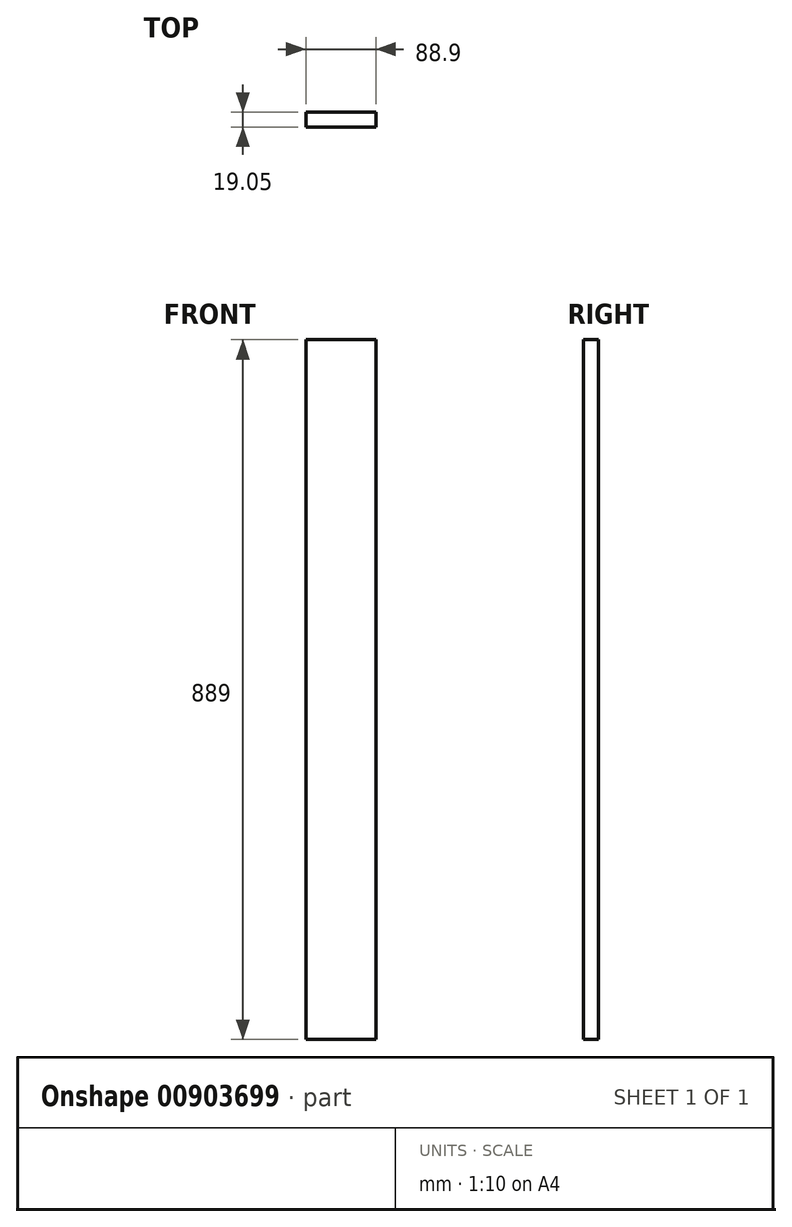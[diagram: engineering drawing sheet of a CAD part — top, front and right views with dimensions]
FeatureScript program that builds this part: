
annotation { "Feature Type Name" : "Feature", "Feature Type Description" : "" }
export const myFeature = defineFeature(function(context is Context, id is Id, definition is map)
    precondition{}
    {
        {
            var Q0;
            Q0=qCreatedBy(makeId("Front.planeOp"),FACE);
            var sketch = newSketch(context, id + "F0", { "sketchPlane" : qUnion([Q0])});
            skLineSegment(sketch, "E0.bottom", {"start": v(-98.48, 624.07) * mm, "end": v(-9.58, 624.07) * mm});
            skLineSegment(sketch, "E0.top", {"start": v(-98.48, -264.93) * mm, "end": v(-9.58, -264.93) * mm});
            skLineSegment(sketch, "E0.left", {"start": v(-98.48, 624.07) * mm, "end": v(-98.48, -264.93) * mm});
            skLineSegment(sketch, "E0.right", {"start": v(-9.58, 624.07) * mm, "end": v(-9.58, -264.93) * mm});
            skSolve(sketch);
        }
        {
            var Q0;
            Q0 = qSketchRegion(id + "F0", true);
            extrude(context, id + "F1", {"entities" : qUnion([Q0]), "depth" : 19.05 * mm, "offsetDistance" : 25.4 * mm});
        }
    });
